# Revit family: LeL Tago 6.1
name_source: partatom
category: Lighting Fixtures
units: mm (PartAtom-declared; Revit-internal decimal feet)

## family parameters
Always vertical = No
Cut with Voids When Loaded = No
Light Source = No
OmniClass Number = 23.80.70.00
OmniClass Title = Lighting
Part Type = Normal
Room Calculation Point = No
Round Connector Dimension = Use Diameter
Shared = No
Work Plane-Based = Yes

## types (6) — shared parameters
CCT = 4000 K
CRI = CRI80
Cable gland dimmable = Yes
Cable gland hint = Switch on cable gland if dimmable
Default Elevation = 1219 mm
Description = Outdoor/linear profiles
Finish = LeL Black
IK = IK09
IP = IP65 IP67 IP69
Lamp = LED
Manufacturer = L&L Luce&Light srl
Model = TG61
URL = https://www.lucelight.it
Weight = 1.88 kg

## per-type parameters (varying)
| type | Apparent Load | Lumen Output | Optic | Rated Power supply | Wattage |
| 6.1 L 52° 24W 48Vdc | 24 VA | 2412 lm | TAGO Light source : 6.1 L 52° 24W 48Vdc | 48 V | 24 W |
| 6.1 M 30° 24W 48Vdc | 24 VA | 2580 lm | TAGO Light source : 6.1 M 30° 24W 48Vdc | 48 V | 24 W |
| 6.1 S 24° 24W 48Vdc | 24 VA | 2748 lm | TAGO Light source : 6.1 S 24° 24W 48Vdc | 48 V | 24 W |
| 6.1 L 52° 29W 230Vac | 29 VA | 2412 lm | TAGO Light source : 6.1 L 52° 29W 230Vac | 230 V | 29 W |
| 6.1 M 30° 29W 230Vac | 29 VA | 2580 lm | TAGO Light source : 6.1 M 30° 29W 230Vac | 230 V | 29 W |
| 6.1 S 24° 29W 230Vac | 29 VA | 2748 lm | TAGO Light source : 6.1 S 24° 29W 230Vac | 230 V | 29 W |

## geometry (parser evidence)
native form markers: Sweep x4
no freeform markers — native parametric forms only
